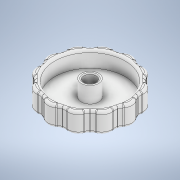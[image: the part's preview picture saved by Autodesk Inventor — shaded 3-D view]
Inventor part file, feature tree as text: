
AUTODESK INVENTOR PART (.ipt)
format: ipt  version: 2022.3 (Build 263350000, 350)  size: 1,125,888 bytes
history: native  units: mm
features: extrude x4, fillet x4, folder x1, pattern_circular x1, sketch x1
ambient origin geometry x8: Origin, YZ Plane, XZ Plane, XY Plane, X Axis, Y Axis, Z Axis, Center Point
bodies: Solid1 (feature_tree)
feature tree (11):
  folder  "Master_sketch"
  extrude  "Extrusion1"  Depth=8.0mm TaperAngle=0.0deg
  extrude  "Extrusion4"  Depth=0.5mm
  fillet  "Fillet4"  Radius=2.0mm
  extrude  "Extrusion5"  Depth=0.5mm
  extrude  "Extrusion3"  Depth=0.5mm TaperAngle=360.0deg
  fillet  "Fillet2"  Radius=1.25mm
  pattern_circular  "Circular Pattern1"  [2 undecoded]
  fillet  "Fillet3"  Radius=1.25mm
  fillet  "Fillet5"  Radius=1.0mm
  sketch  "Sketch3"  dims[d0=35.0mm d12=8.0mm d13=0.0mm d14=2.0mm d18=2.0mm d19=0.0mm d20=5.0mm d21=120.0mm d22=360.0deg d24=1.25mm d27=6.25mm d28=1.25mm d30=1.0mm d31=7.0mm d32=0.0mm d33=0.5mm d34=2.0mm d35=0.0mm d36=8.0mm d37=0.0mm d38=0.5mm d29=0.5mm d39=0.5mm d40=0.872665mm d41=0.5mm d42=0.872665mm]
note: 2 required parameter values undecoded (feature->parameter linkage not recoverable at this tier; creation-order binding heuristic only, values carry confidence <= 0.55)
